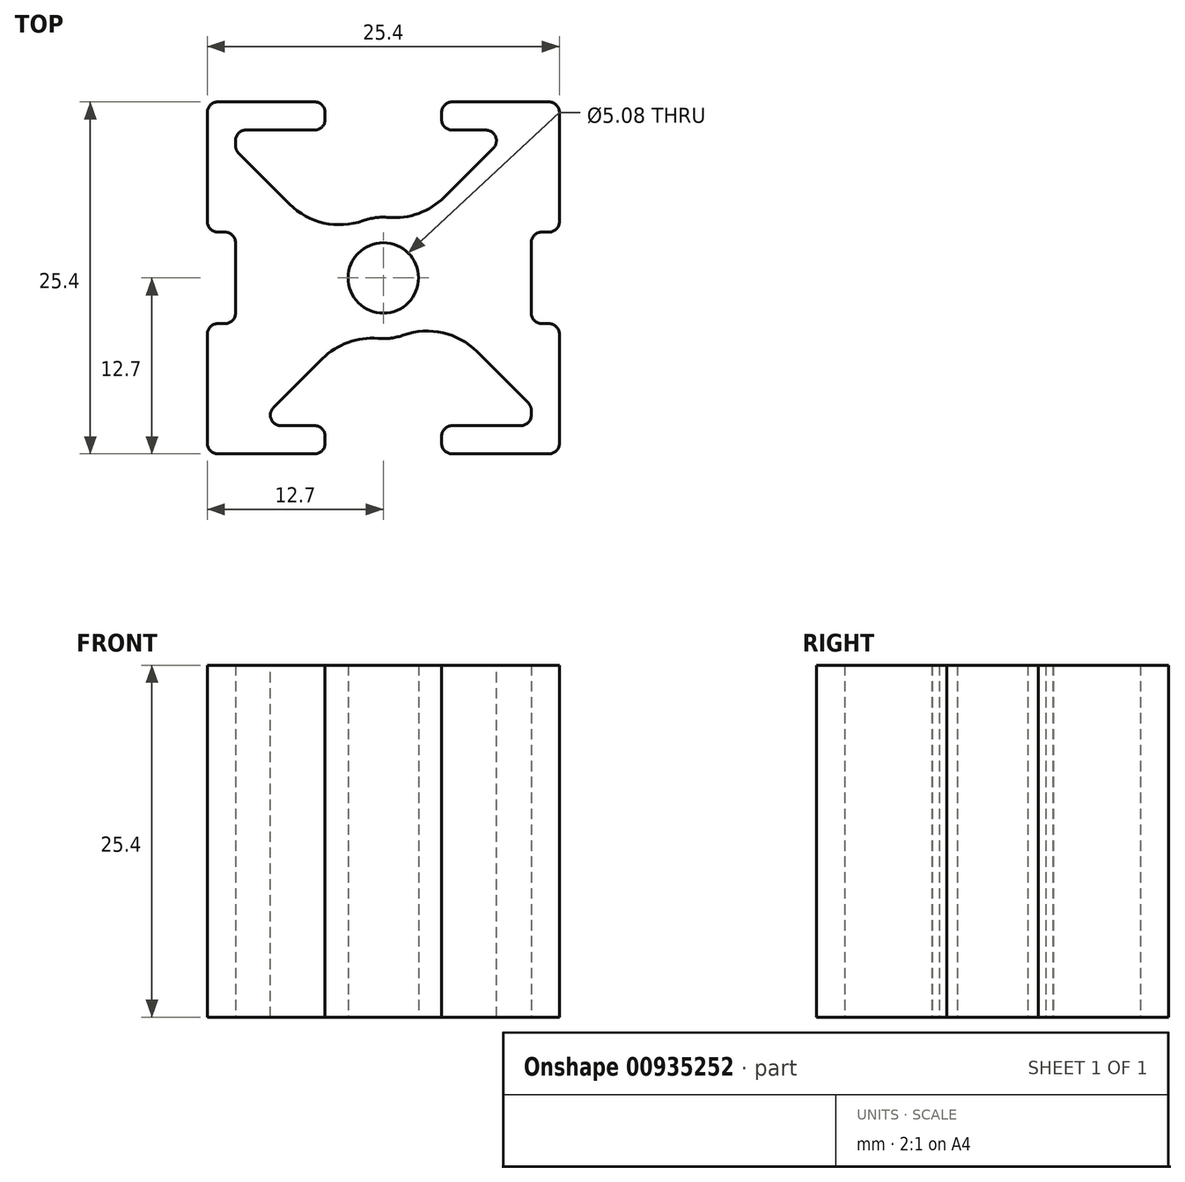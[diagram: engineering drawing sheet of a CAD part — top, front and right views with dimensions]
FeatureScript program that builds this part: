
annotation { "Feature Type Name" : "Feature", "Feature Type Description" : "" }
export const myFeature = defineFeature(function(context is Context, id is Id, definition is map)
    precondition{}
    {
        {
            var Q0;
            Q0=qCreatedBy(makeId("Top.planeOp"),FACE);
            var sketch = newSketch(context, id + "F0", { "sketchPlane" : qUnion([Q0])});
            skLineSegment(sketch, "E0.bottom", {"start": v(12.7, -12.7) * mm, "end": v(-12.7, -12.7) * mm});
            skLineSegment(sketch, "E0.top", {"start": v(12.7, 12.7) * mm, "end": v(-12.7, 12.7) * mm});
            skLineSegment(sketch, "E0.left", {"start": v(12.7, -12.7) * mm, "end": v(12.7, 12.7) * mm});
            skLineSegment(sketch, "E0.right", {"start": v(-12.7, -12.7) * mm, "end": v(-12.7, 12.7) * mm});
            skPoint(sketch, "E0.middle", {"position": v(0, 0) * mm});
            skCircle(sketch, "E1", {"center": v(0, 0) * mm, "radius": 2.54 * mm});
            skCircle(sketch, "E2", {"center": v(0, 0) * mm, "radius": 4.38 * mm});
            skLineSegment(sketch, "E3", {"start": v(-12.7, 12.7) * mm, "end": v(12.7, -12.7) * mm, "construction": true});
            skLineSegment(sketch, "E4", {"start": v(-12.7, -12.7) * mm, "end": v(12.7, 12.7) * mm, "construction": true});
            skLineSegment(sketch, "E5", {"start": v(-12.7, 0) * mm, "end": v(12.7, 0) * mm, "construction": true});
            skLineSegment(sketch, "E6", {"start": v(0, 12.7) * mm, "end": v(0, -12.7) * mm, "construction": true});
            skLineSegment(sketch, "E7.0", {"start": v(10.67, 10.67) * mm, "end": v(-10.67, 10.67) * mm});
            skLineSegment(sketch, "E7.1", {"start": v(10.67, -10.67) * mm, "end": v(10.67, 10.67) * mm});
            skLineSegment(sketch, "E7.2", {"start": v(10.67, -10.67) * mm, "end": v(-10.67, -10.67) * mm});
            skLineSegment(sketch, "E7.3", {"start": v(-10.67, -10.67) * mm, "end": v(-10.67, 10.67) * mm});
            skLineSegment(sketch, "E8.bottom", {"start": v(-10.67, 3.3) * mm, "end": v(-14.73, 3.3) * mm});
            skLineSegment(sketch, "E8.top", {"start": v(-10.67, -3.3) * mm, "end": v(-14.73, -3.3) * mm});
            skLineSegment(sketch, "E8.left", {"start": v(-10.67, 3.3) * mm, "end": v(-10.67, -3.3) * mm});
            skLineSegment(sketch, "E8.right", {"start": v(-14.73, 3.3) * mm, "end": v(-14.73, -3.3) * mm});
            skPoint(sketch, "E8.middle", {"position": v(-12.7, 0) * mm});
            skLineSegment(sketch, "E9.bottom", {"start": v(4.2, 10.67) * mm, "end": v(-4.2, 10.67) * mm});
            skLineSegment(sketch, "E9.top", {"start": v(4.2, 14.73) * mm, "end": v(-4.2, 14.73) * mm});
            skLineSegment(sketch, "E9.left", {"start": v(4.2, 10.67) * mm, "end": v(4.2, 14.73) * mm});
            skLineSegment(sketch, "E9.right", {"start": v(-4.2, 10.67) * mm, "end": v(-4.2, 14.73) * mm});
            skPoint(sketch, "E9.middle", {"position": v(0, 12.7) * mm});
            skLineSegment(sketch, "E10.0", {"start": v(-13.42, 11.98) * mm, "end": v(11.98, -13.42) * mm});
            skLineSegment(sketch, "E11.0", {"start": v(-11.98, 13.42) * mm, "end": v(13.42, -11.98) * mm});
            skLineSegment(sketch, "E12.MirrorCS", {"start": v(10.67, 3.3) * mm, "end": v(14.73, 3.3) * mm});
            skLineSegment(sketch, "E13.MirrorCS", {"start": v(10.67, -3.3) * mm, "end": v(14.73, -3.3) * mm});
            skLineSegment(sketch, "E14.MirrorCS", {"start": v(14.73, 3.3) * mm, "end": v(14.73, -3.3) * mm});
            skLineSegment(sketch, "E15.MirrorCS", {"start": v(4.2, -14.73) * mm, "end": v(-4.2, -14.73) * mm});
            skLineSegment(sketch, "E16.MirrorCS", {"start": v(-4.2, -10.67) * mm, "end": v(-4.2, -14.73) * mm});
            skLineSegment(sketch, "E17.MirrorCS", {"start": v(4.2, -10.67) * mm, "end": v(4.2, -14.73) * mm});
            skLineSegment(sketch, "E18.0", {"start": v(-11.98, -13.42) * mm, "end": v(13.42, 11.98) * mm});
            skLineSegment(sketch, "E19.0", {"start": v(-13.42, -11.98) * mm, "end": v(11.98, 13.42) * mm});
            skSolve(sketch);
        }
        {
            var Q0;
            {var subQ0=sQuery(id+"F0.wireOp",EDGE,"E11.0");var subQ1=sQuery(id+"F0.wireOp",EDGE,"E0.top");var subQ2=makeQuery(id+"F0.imprint","INTERSECT",VERTEX,{"derivedFrom":[subQ1,subQ0]});Q0=makeQuery(id+"F0.imprint","IMPRINT",FACE,{"disambiguationData":[TD([[makeQuery(id+"F0.imprint","IMPRINT",EDGE,{"disambiguationData":[TD([[subQ2,1.0]])],"derivedFrom":subQ1}),1.0]])]});}
            var Q1;
            {var subQ5=sQuery(id+"F0.wireOp",EDGE,"E0.right");var subQ6=sQuery(id+"F0.wireOp",EDGE,"E0.top");var subQ7=makeQuery(id+"F0.imprint","INTERSECT",VERTEX,{"derivedFrom":[subQ6,subQ5]});Q1=makeQuery(id+"F0.imprint","IMPRINT",FACE,{"disambiguationData":[TD([[makeQuery(id+"F0.imprint","IMPRINT",EDGE,{"disambiguationData":[TD([[subQ7,1.0]])],"derivedFrom":subQ6}),1.0]])]});}
            var Q2;
            {var subQ0=sQuery(id+"F0.wireOp",EDGE,"E10.0");var subQ1=sQuery(id+"F0.wireOp",EDGE,"E0.right");var subQ2=makeQuery(id+"F0.imprint","INTERSECT",VERTEX,{"derivedFrom":[subQ1,subQ0]});Q2=makeQuery(id+"F0.imprint","IMPRINT",FACE,{"disambiguationData":[TD([[makeQuery(id+"F0.imprint","IMPRINT",EDGE,{"disambiguationData":[TD([[subQ2,1.0]])],"derivedFrom":subQ1}),-1.0]])]});}
            var Q3;
            {var subQ0=sQuery(id+"F0.wireOp",EDGE,"E19.0");var subQ1=sQuery(id+"F0.wireOp",EDGE,"E0.right");var subQ2=makeQuery(id+"F0.imprint","INTERSECT",VERTEX,{"derivedFrom":[subQ1,subQ0]});Q3=makeQuery(id+"F0.imprint","IMPRINT",FACE,{"disambiguationData":[TD([[makeQuery(id+"F0.imprint","IMPRINT",EDGE,{"disambiguationData":[TD([[subQ2,-1.0]])],"derivedFrom":subQ1}),-1.0]])]});}
            var Q4;
            {var subQ6=sQuery(id+"F0.wireOp",EDGE,"E0.bottom");var subQ9=sQuery(id+"F0.wireOp",EDGE,"E0.right");var subQ10=makeQuery(id+"F0.imprint","INTERSECT",VERTEX,{"derivedFrom":[subQ6,subQ9]});Q4=makeQuery(id+"F0.imprint","IMPRINT",FACE,{"disambiguationData":[TD([[makeQuery(id+"F0.imprint","IMPRINT",EDGE,{"disambiguationData":[TD([[subQ10,1.0]])],"derivedFrom":subQ6}),-1.0]])]});}
            var Q5;
            {var subQ0=sQuery(id+"F0.wireOp",EDGE,"E18.0");var subQ1=sQuery(id+"F0.wireOp",EDGE,"E0.bottom");var subQ2=makeQuery(id+"F0.imprint","INTERSECT",VERTEX,{"derivedFrom":[subQ1,subQ0]});Q5=makeQuery(id+"F0.imprint","IMPRINT",FACE,{"disambiguationData":[TD([[makeQuery(id+"F0.imprint","IMPRINT",EDGE,{"disambiguationData":[TD([[subQ2,1.0]])],"derivedFrom":subQ1}),-1.0]])]});}
            var Q6;
            {var subQ0=sQuery(id+"F0.wireOp",EDGE,"E10.0");var subQ1=sQuery(id+"F0.wireOp",EDGE,"E0.bottom");var subQ2=makeQuery(id+"F0.imprint","INTERSECT",VERTEX,{"derivedFrom":[subQ1,subQ0]});Q6=makeQuery(id+"F0.imprint","IMPRINT",FACE,{"disambiguationData":[TD([[makeQuery(id+"F0.imprint","IMPRINT",EDGE,{"disambiguationData":[TD([[subQ2,-1.0]])],"derivedFrom":subQ1}),-1.0]])]});}
            var Q7;
            {var subQ7=sQuery(id+"F0.wireOp",EDGE,"E0.left");var subQ8=sQuery(id+"F0.wireOp",EDGE,"E0.bottom");var subQ9=makeQuery(id+"F0.imprint","INTERSECT",VERTEX,{"derivedFrom":[subQ8,subQ7]});Q7=makeQuery(id+"F0.imprint","IMPRINT",FACE,{"disambiguationData":[TD([[makeQuery(id+"F0.imprint","IMPRINT",EDGE,{"disambiguationData":[TD([[subQ9,-1.0]])],"derivedFrom":subQ8}),-1.0]])]});}
            var Q8;
            {var subQ0=sQuery(id+"F0.wireOp",EDGE,"E11.0");var subQ1=sQuery(id+"F0.wireOp",EDGE,"E0.left");var subQ2=makeQuery(id+"F0.imprint","INTERSECT",VERTEX,{"derivedFrom":[subQ1,subQ0]});Q8=makeQuery(id+"F0.imprint","IMPRINT",FACE,{"disambiguationData":[TD([[makeQuery(id+"F0.imprint","IMPRINT",EDGE,{"disambiguationData":[TD([[subQ2,-1.0]])],"derivedFrom":subQ1}),1.0]])]});}
            var Q9;
            {var subQ0=sQuery(id+"F0.wireOp",EDGE,"E18.0");var subQ1=sQuery(id+"F0.wireOp",EDGE,"E0.left");var subQ2=makeQuery(id+"F0.imprint","INTERSECT",VERTEX,{"derivedFrom":[subQ1,subQ0]});Q9=makeQuery(id+"F0.imprint","IMPRINT",FACE,{"disambiguationData":[TD([[makeQuery(id+"F0.imprint","IMPRINT",EDGE,{"disambiguationData":[TD([[subQ2,1.0]])],"derivedFrom":subQ1}),1.0]])]});}
            var Q10;
            {var subQ5=sQuery(id+"F0.wireOp",EDGE,"E0.left");var subQ6=sQuery(id+"F0.wireOp",EDGE,"E0.top");var subQ7=makeQuery(id+"F0.imprint","INTERSECT",VERTEX,{"derivedFrom":[subQ6,subQ5]});Q10=makeQuery(id+"F0.imprint","IMPRINT",FACE,{"disambiguationData":[TD([[makeQuery(id+"F0.imprint","IMPRINT",EDGE,{"disambiguationData":[TD([[subQ7,-1.0]])],"derivedFrom":subQ6}),1.0]])]});}
            var Q11;
            {var subQ0=sQuery(id+"F0.wireOp",EDGE,"E19.0");var subQ1=sQuery(id+"F0.wireOp",EDGE,"E0.top");var subQ2=makeQuery(id+"F0.imprint","INTERSECT",VERTEX,{"derivedFrom":[subQ1,subQ0]});Q11=makeQuery(id+"F0.imprint","IMPRINT",FACE,{"disambiguationData":[TD([[makeQuery(id+"F0.imprint","IMPRINT",EDGE,{"disambiguationData":[TD([[subQ2,-1.0]])],"derivedFrom":subQ1}),1.0]])]});}
            var Q12;
            {var subQ1=sQuery(id+"F0.wireOp",EDGE,"E2");var subQ7=sQuery(id+"F0.wireOp",EDGE,"E11.0");var subQ9=makeQuery(id+"F0.imprint","INTERSECT",VERTEX,{"disambiguationData":[OD(0.0)],"derivedFrom":[subQ1,subQ7]});Q12=makeQuery(id+"F0.imprint","IMPRINT",FACE,{"disambiguationData":[TD([[makeQuery(id+"F0.imprint","IMPRINT",EDGE,{"disambiguationData":[TD([[subQ9,-1.0]])],"derivedFrom":subQ1}),-1.0]])]});}
            var Q13;
            {var subQ5=sQuery(id+"F0.wireOp",EDGE,"E19.0");var subQ6=sQuery(id+"F0.wireOp",EDGE,"E2");var subQ7=makeQuery(id+"F0.imprint","INTERSECT",VERTEX,{"disambiguationData":[OD(0.0)],"derivedFrom":[subQ6,subQ5]});Q13=makeQuery(id+"F0.imprint","IMPRINT",FACE,{"disambiguationData":[TD([[makeQuery(id+"F0.imprint","IMPRINT",EDGE,{"disambiguationData":[TD([[subQ7,1.0]])],"derivedFrom":subQ6}),-1.0]])]});}
            var Q14;
            {var subQ1=sQuery(id+"F0.wireOp",EDGE,"E2");var subQ7=sQuery(id+"F0.wireOp",EDGE,"E19.0");var subQ9=makeQuery(id+"F0.imprint","INTERSECT",VERTEX,{"disambiguationData":[OD(1.0)],"derivedFrom":[subQ1,subQ7]});Q14=makeQuery(id+"F0.imprint","IMPRINT",FACE,{"disambiguationData":[TD([[makeQuery(id+"F0.imprint","IMPRINT",EDGE,{"disambiguationData":[TD([[subQ9,-1.0]])],"derivedFrom":subQ1}),-1.0]])]});}
            var Q15;
            {var subQ0=sQuery(id+"F0.wireOp",EDGE,"E10.0");var subQ1=sQuery(id+"F0.wireOp",EDGE,"E2");var subQ2=makeQuery(id+"F0.imprint","INTERSECT",VERTEX,{"disambiguationData":[OD(1.0)],"derivedFrom":[subQ1,subQ0]});Q15=makeQuery(id+"F0.imprint","IMPRINT",FACE,{"disambiguationData":[TD([[makeQuery(id+"F0.imprint","IMPRINT",EDGE,{"disambiguationData":[TD([[subQ2,-1.0]])],"derivedFrom":subQ1}),-1.0]])]});}
            var Q16;
            {var subQ0=sQuery(id+"F0.wireOp",EDGE,"E19.0");var subQ1=sQuery(id+"F0.wireOp",EDGE,"E1");var subQ2=makeQuery(id+"F0.imprint","INTERSECT",VERTEX,{"disambiguationData":[OD(0.0)],"derivedFrom":[subQ1,subQ0]});Q16=makeQuery(id+"F0.imprint","IMPRINT",FACE,{"disambiguationData":[TD([[makeQuery(id+"F0.imprint","IMPRINT",EDGE,{"disambiguationData":[TD([[subQ2,-1.0]])],"derivedFrom":subQ1}),-1.0]])]});}
            var Q17;
            {var subQ0=sQuery(id+"F0.wireOp",EDGE,"E11.0");var subQ1=sQuery(id+"F0.wireOp",EDGE,"E1");var subQ2=makeQuery(id+"F0.imprint","INTERSECT",VERTEX,{"disambiguationData":[OD(0.0)],"derivedFrom":[subQ1,subQ0]});Q17=makeQuery(id+"F0.imprint","IMPRINT",FACE,{"disambiguationData":[TD([[makeQuery(id+"F0.imprint","IMPRINT",EDGE,{"disambiguationData":[TD([[subQ2,-1.0]])],"derivedFrom":subQ1}),-1.0]])]});}
            var Q18;
            {var subQ0=sQuery(id+"F0.wireOp",EDGE,"E10.0");var subQ1=sQuery(id+"F0.wireOp",EDGE,"E1");var subQ2=makeQuery(id+"F0.imprint","INTERSECT",VERTEX,{"disambiguationData":[OD(0.0)],"derivedFrom":[subQ1,subQ0]});Q18=makeQuery(id+"F0.imprint","IMPRINT",FACE,{"disambiguationData":[TD([[makeQuery(id+"F0.imprint","IMPRINT",EDGE,{"disambiguationData":[TD([[subQ2,-1.0]])],"derivedFrom":subQ1}),-1.0]])]});}
            var Q19;
            {var subQ0=sQuery(id+"F0.wireOp",EDGE,"E19.0");var subQ1=sQuery(id+"F0.wireOp",EDGE,"E1");var subQ2=makeQuery(id+"F0.imprint","INTERSECT",VERTEX,{"disambiguationData":[OD(1.0)],"derivedFrom":[subQ1,subQ0]});Q19=makeQuery(id+"F0.imprint","IMPRINT",FACE,{"disambiguationData":[TD([[makeQuery(id+"F0.imprint","IMPRINT",EDGE,{"disambiguationData":[TD([[subQ2,-1.0]])],"derivedFrom":subQ1}),-1.0]])]});}
            var Q20;
            {var subQ0=sQuery(id+"F0.wireOp",EDGE,"E18.0");var subQ1=sQuery(id+"F0.wireOp",EDGE,"E1");var subQ2=makeQuery(id+"F0.imprint","INTERSECT",VERTEX,{"disambiguationData":[OD(1.0)],"derivedFrom":[subQ1,subQ0]});Q20=makeQuery(id+"F0.imprint","IMPRINT",FACE,{"disambiguationData":[TD([[makeQuery(id+"F0.imprint","IMPRINT",EDGE,{"disambiguationData":[TD([[subQ2,-1.0]])],"derivedFrom":subQ1}),-1.0]])]});}
            var Q21;
            {var subQ0=sQuery(id+"F0.wireOp",EDGE,"E19.0");var subQ1=sQuery(id+"F0.wireOp",EDGE,"E1");var subQ2=makeQuery(id+"F0.imprint","INTERSECT",VERTEX,{"disambiguationData":[OD(0.0)],"derivedFrom":[subQ1,subQ0]});Q21=makeQuery(id+"F0.imprint","IMPRINT",FACE,{"disambiguationData":[TD([[makeQuery(id+"F0.imprint","IMPRINT",EDGE,{"disambiguationData":[TD([[subQ2,1.0]])],"derivedFrom":subQ1}),-1.0]])]});}
            var Q22;
            {var subQ0=sQuery(id+"F0.wireOp",EDGE,"E18.0");var subQ1=sQuery(id+"F0.wireOp",EDGE,"E1");var subQ2=makeQuery(id+"F0.imprint","INTERSECT",VERTEX,{"disambiguationData":[OD(0.0)],"derivedFrom":[subQ1,subQ0]});Q22=makeQuery(id+"F0.imprint","IMPRINT",FACE,{"disambiguationData":[TD([[makeQuery(id+"F0.imprint","IMPRINT",EDGE,{"disambiguationData":[TD([[subQ2,1.0]])],"derivedFrom":subQ1}),-1.0]])]});}
            var Q23;
            {var subQ0=sQuery(id+"F0.wireOp",EDGE,"E10.0");var subQ1=sQuery(id+"F0.wireOp",EDGE,"E1");var subQ2=makeQuery(id+"F0.imprint","INTERSECT",VERTEX,{"disambiguationData":[OD(1.0)],"derivedFrom":[subQ1,subQ0]});Q23=makeQuery(id+"F0.imprint","IMPRINT",FACE,{"disambiguationData":[TD([[makeQuery(id+"F0.imprint","IMPRINT",EDGE,{"disambiguationData":[TD([[subQ2,-1.0]])],"derivedFrom":subQ1}),-1.0]])]});}
            extrude(context, id + "F1", {"entities" : qUnion([Q0, Q1, Q2, Q3, Q4, Q5, Q6, Q7, Q8, Q9, Q10, Q11, Q12, Q13, Q14, Q15, Q16, Q17, Q18, Q19, Q20, Q21, Q22, Q23]), "depth" : 25.4 * mm, "offsetDistance" : 25.4 * mm});
        }
        {
            var Q0;
            {var subQ0=sQuery(id+"F0.wireOp",EDGE,"E10.0");var subQ1=sQuery(id+"F0.wireOp",EDGE,"E2");Q0=makeQuery(id+"F1.opExtrude","SWEPT_EDGE",EDGE,{"disambiguationData":[OSD([subQ1,subQ0]),TDD([makeQuery(id+"F0.imprint","INTERSECT",VERTEX,{"disambiguationData":[OD(0.0)],"derivedFrom":[subQ1,subQ0]})])]});}
            var Q1;
            {var subQ0=sQuery(id+"F0.wireOp",EDGE,"E19.0");var subQ1=sQuery(id+"F0.wireOp",EDGE,"E2");Q1=makeQuery(id+"F1.opExtrude","SWEPT_EDGE",EDGE,{"disambiguationData":[OSD([subQ1,subQ0]),TDD([makeQuery(id+"F0.imprint","INTERSECT",VERTEX,{"disambiguationData":[OD(1.0)],"derivedFrom":[subQ1,subQ0]})])]});}
            var Q2;
            {var subQ0=sQuery(id+"F0.wireOp",EDGE,"E11.0");var subQ1=sQuery(id+"F0.wireOp",EDGE,"E2");Q2=makeQuery(id+"F1.opExtrude","SWEPT_EDGE",EDGE,{"disambiguationData":[OSD([subQ1,subQ0]),TDD([makeQuery(id+"F0.imprint","INTERSECT",VERTEX,{"disambiguationData":[OD(0.0)],"derivedFrom":[subQ1,subQ0]})])]});}
            var Q3;
            {var subQ0=sQuery(id+"F0.wireOp",EDGE,"E19.0");var subQ1=sQuery(id+"F0.wireOp",EDGE,"E2");Q3=makeQuery(id+"F1.opExtrude","SWEPT_EDGE",EDGE,{"disambiguationData":[OSD([subQ1,subQ0]),TDD([makeQuery(id+"F0.imprint","INTERSECT",VERTEX,{"disambiguationData":[OD(0.0)],"derivedFrom":[subQ1,subQ0]})])]});}
            var Q4;
            {var subQ0=sQuery(id+"F0.wireOp",EDGE,"E18.0");var subQ1=sQuery(id+"F0.wireOp",EDGE,"E2");Q4=makeQuery(id+"F1.opExtrude","SWEPT_EDGE",EDGE,{"disambiguationData":[OSD([subQ1,subQ0]),TDD([makeQuery(id+"F0.imprint","INTERSECT",VERTEX,{"disambiguationData":[OD(1.0)],"derivedFrom":[subQ1,subQ0]})])]});}
            var Q5;
            {var subQ0=sQuery(id+"F0.wireOp",EDGE,"E10.0");var subQ1=sQuery(id+"F0.wireOp",EDGE,"E2");Q5=makeQuery(id+"F1.opExtrude","SWEPT_EDGE",EDGE,{"disambiguationData":[OSD([subQ1,subQ0]),TDD([makeQuery(id+"F0.imprint","INTERSECT",VERTEX,{"disambiguationData":[OD(1.0)],"derivedFrom":[subQ1,subQ0]})])]});}
            var Q6;
            {var subQ0=sQuery(id+"F0.wireOp",EDGE,"E11.0");var subQ1=sQuery(id+"F0.wireOp",EDGE,"E2");Q6=makeQuery(id+"F1.opExtrude","SWEPT_EDGE",EDGE,{"disambiguationData":[OSD([subQ1,subQ0]),TDD([makeQuery(id+"F0.imprint","INTERSECT",VERTEX,{"disambiguationData":[OD(1.0)],"derivedFrom":[subQ1,subQ0]})])]});}
            var Q7;
            {var subQ0=sQuery(id+"F0.wireOp",EDGE,"E18.0");var subQ1=sQuery(id+"F0.wireOp",EDGE,"E2");Q7=makeQuery(id+"F1.opExtrude","SWEPT_EDGE",EDGE,{"disambiguationData":[OSD([subQ1,subQ0]),TDD([makeQuery(id+"F0.imprint","INTERSECT",VERTEX,{"disambiguationData":[OD(0.0)],"derivedFrom":[subQ1,subQ0]})])]});}
            fillet(context, id + "F2", {"entities" : qUnion([Q0, Q1, Q2, Q3, Q4, Q5, Q6, Q7]), "radius" : 5.08 * mm, "tangentPropagation" : true, "allowEdgeOverflow" : false});
        }
        {
            var Q0;
            Q0=makeQuery(id+"F1.opExtrude","SWEPT_EDGE",EDGE,{"disambiguationData":[OSD([sQuery(id+"F0.wireOp",EDGE,"E7.0"),sQuery(id+"F0.wireOp",EDGE,"E19.0")])]});
            var Q1;
            Q1=makeQuery(id+"F1.opExtrude","SWEPT_EDGE",EDGE,{"disambiguationData":[OSD([sQuery(id+"F0.wireOp",EDGE,"E7.1"),sQuery(id+"F0.wireOp",EDGE,"E18.0")])]});
            var Q2;
            Q2=makeQuery(id+"F1.opExtrude","SWEPT_EDGE",EDGE,{"disambiguationData":[OSD([sQuery(id+"F0.wireOp",EDGE,"E7.0"),sQuery(id+"F0.wireOp",EDGE,"E11.0")])]});
            var Q3;
            Q3=makeQuery(id+"F1.opExtrude","SWEPT_EDGE",EDGE,{"disambiguationData":[OSD([sQuery(id+"F0.wireOp",EDGE,"E7.3"),sQuery(id+"F0.wireOp",EDGE,"E10.0")])]});
            var Q4;
            Q4=makeQuery(id+"F1.opExtrude","SWEPT_EDGE",EDGE,{"disambiguationData":[OSD([sQuery(id+"F0.wireOp",EDGE,"E7.1"),sQuery(id+"F0.wireOp",EDGE,"E11.0")])]});
            var Q5;
            Q5=makeQuery(id+"F1.opExtrude","SWEPT_EDGE",EDGE,{"disambiguationData":[OSD([sQuery(id+"F0.wireOp",EDGE,"E7.2"),sQuery(id+"F0.wireOp",EDGE,"E10.0")])]});
            var Q6;
            Q6=makeQuery(id+"F1.opExtrude","SWEPT_EDGE",EDGE,{"disambiguationData":[OSD([sQuery(id+"F0.wireOp",EDGE,"E7.2"),sQuery(id+"F0.wireOp",EDGE,"E18.0")])]});
            var Q7;
            Q7=makeQuery(id+"F1.opExtrude","SWEPT_EDGE",EDGE,{"disambiguationData":[OSD([sQuery(id+"F0.wireOp",EDGE,"E7.3"),sQuery(id+"F0.wireOp",EDGE,"E19.0")])]});
            var Q8;
            Q8=makeQuery(id+"F1.opExtrude","SWEPT_EDGE",EDGE,{"disambiguationData":[OSD([sQuery(id+"F0.wireOp",EDGE,"E0.top"),sQuery(id+"F0.wireOp",EDGE,"E0.right")])]});
            var Q9;
            Q9=makeQuery(id+"F1.opExtrude","SWEPT_EDGE",EDGE,{"disambiguationData":[OSD([sQuery(id+"F0.wireOp",EDGE,"E0.top"),sQuery(id+"F0.wireOp",EDGE,"E0.left")])]});
            var Q10;
            Q10=makeQuery(id+"F1.opExtrude","SWEPT_EDGE",EDGE,{"disambiguationData":[OSD([sQuery(id+"F0.wireOp",EDGE,"E0.bottom"),sQuery(id+"F0.wireOp",EDGE,"E0.left")])]});
            var Q11;
            Q11=makeQuery(id+"F1.opExtrude","SWEPT_EDGE",EDGE,{"disambiguationData":[OSD([sQuery(id+"F0.wireOp",EDGE,"E0.bottom"),sQuery(id+"F0.wireOp",EDGE,"E0.right")])]});
            var Q12;
            Q12=makeQuery(id+"F1.opExtrude","SWEPT_EDGE",EDGE,{"disambiguationData":[OSD([sQuery(id+"F0.wireOp",EDGE,"E0.left"),sQuery(id+"F0.wireOp",EDGE,"E12.MirrorCS")])]});
            var Q13;
            Q13=makeQuery(id+"F1.opExtrude","SWEPT_EDGE",EDGE,{"disambiguationData":[OSD([sQuery(id+"F0.wireOp",EDGE,"E7.1"),sQuery(id+"F0.wireOp",EDGE,"E12.MirrorCS")])]});
            var Q14;
            Q14=makeQuery(id+"F1.opExtrude","SWEPT_EDGE",EDGE,{"disambiguationData":[OSD([sQuery(id+"F0.wireOp",EDGE,"E7.0"),sQuery(id+"F0.wireOp",EDGE,"E9.bottom"),sQuery(id+"F0.wireOp",EDGE,"E9.left")])]});
            var Q15;
            Q15=makeQuery(id+"F1.opExtrude","SWEPT_EDGE",EDGE,{"disambiguationData":[OSD([sQuery(id+"F0.wireOp",EDGE,"E0.top"),sQuery(id+"F0.wireOp",EDGE,"E9.left")])]});
            var Q16;
            Q16=makeQuery(id+"F1.opExtrude","SWEPT_EDGE",EDGE,{"disambiguationData":[OSD([sQuery(id+"F0.wireOp",EDGE,"E0.top"),sQuery(id+"F0.wireOp",EDGE,"E9.right")])]});
            var Q17;
            Q17=makeQuery(id+"F1.opExtrude","SWEPT_EDGE",EDGE,{"disambiguationData":[OSD([sQuery(id+"F0.wireOp",EDGE,"E7.0"),sQuery(id+"F0.wireOp",EDGE,"E9.bottom"),sQuery(id+"F0.wireOp",EDGE,"E9.right")])]});
            var Q18;
            Q18=makeQuery(id+"F1.opExtrude","SWEPT_EDGE",EDGE,{"disambiguationData":[OSD([sQuery(id+"F0.wireOp",EDGE,"E7.3"),sQuery(id+"F0.wireOp",EDGE,"E8.bottom"),sQuery(id+"F0.wireOp",EDGE,"E8.left")])]});
            var Q19;
            Q19=makeQuery(id+"F1.opExtrude","SWEPT_EDGE",EDGE,{"disambiguationData":[OSD([sQuery(id+"F0.wireOp",EDGE,"E0.right"),sQuery(id+"F0.wireOp",EDGE,"E8.bottom")])]});
            var Q20;
            Q20=makeQuery(id+"F1.opExtrude","SWEPT_EDGE",EDGE,{"disambiguationData":[OSD([sQuery(id+"F0.wireOp",EDGE,"E7.3"),sQuery(id+"F0.wireOp",EDGE,"E8.top"),sQuery(id+"F0.wireOp",EDGE,"E8.left")])]});
            var Q21;
            Q21=makeQuery(id+"F1.opExtrude","SWEPT_EDGE",EDGE,{"disambiguationData":[OSD([sQuery(id+"F0.wireOp",EDGE,"E0.right"),sQuery(id+"F0.wireOp",EDGE,"E8.top")])]});
            var Q22;
            Q22=makeQuery(id+"F1.opExtrude","SWEPT_EDGE",EDGE,{"disambiguationData":[OSD([sQuery(id+"F0.wireOp",EDGE,"E7.2"),sQuery(id+"F0.wireOp",EDGE,"E17.MirrorCS")])]});
            var Q23;
            Q23=makeQuery(id+"F1.opExtrude","SWEPT_EDGE",EDGE,{"disambiguationData":[OSD([sQuery(id+"F0.wireOp",EDGE,"E0.bottom"),sQuery(id+"F0.wireOp",EDGE,"E17.MirrorCS")])]});
            var Q24;
            Q24=makeQuery(id+"F1.opExtrude","SWEPT_EDGE",EDGE,{"disambiguationData":[OSD([sQuery(id+"F0.wireOp",EDGE,"E7.1"),sQuery(id+"F0.wireOp",EDGE,"E13.MirrorCS")])]});
            var Q25;
            Q25=makeQuery(id+"F1.opExtrude","SWEPT_EDGE",EDGE,{"disambiguationData":[OSD([sQuery(id+"F0.wireOp",EDGE,"E0.left"),sQuery(id+"F0.wireOp",EDGE,"E13.MirrorCS")])]});
            var Q26;
            Q26=makeQuery(id+"F1.opExtrude","SWEPT_EDGE",EDGE,{"disambiguationData":[OSD([sQuery(id+"F0.wireOp",EDGE,"E0.bottom"),sQuery(id+"F0.wireOp",EDGE,"E16.MirrorCS")])]});
            var Q27;
            Q27=makeQuery(id+"F1.opExtrude","SWEPT_EDGE",EDGE,{"disambiguationData":[OSD([sQuery(id+"F0.wireOp",EDGE,"E7.2"),sQuery(id+"F0.wireOp",EDGE,"E16.MirrorCS")])]});
            fillet(context, id + "F3", {"entities" : qUnion([Q0, Q1, Q2, Q3, Q4, Q5, Q6, Q7, Q8, Q9, Q10, Q11, Q12, Q13, Q14, Q15, Q16, Q17, Q18, Q19, Q20, Q21, Q22, Q23, Q24, Q25, Q26, Q27]), "radius" : 0.76 * mm, "tangentPropagation" : true, "allowEdgeOverflow" : false});
        }
    });
